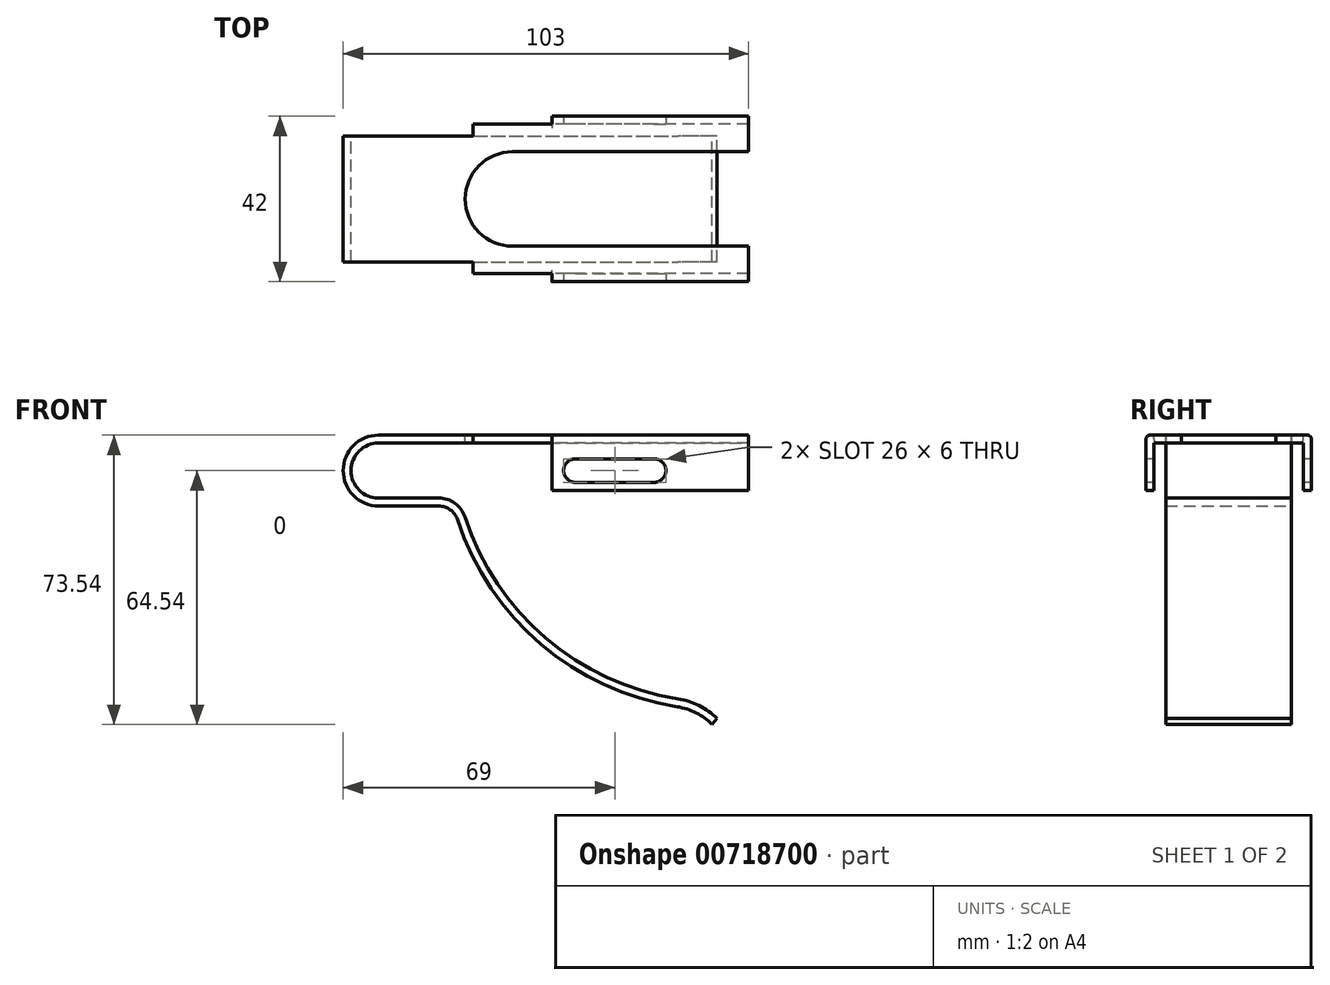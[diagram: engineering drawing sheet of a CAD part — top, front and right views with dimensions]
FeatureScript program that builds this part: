
annotation { "Feature Type Name" : "Feature", "Feature Type Description" : "" }
export const myFeature = defineFeature(function(context is Context, id is Id, definition is map)
    precondition{}
    {
        {
            var Q0;
            Q0=qCreatedBy(makeId("Front.planeOp"),FACE);
            var sketch = newSketch(context, id + "F0", { "sketchPlane" : qUnion([Q0])});
            skArc(sketch, "E0", {"start": v(0, 9) * mm, "mid": v(-9, 0) * mm, "end": v(0, -9) * mm});
            skLineSegment(sketch, "E1", {"start": v(0, 9) * mm, "end": v(94, 9) * mm});
            skLineSegment(sketch, "E2", {"start": v(0, -9) * mm, "end": v(15.27, -9) * mm});
            skArc(sketch, "E3", {"start": v(20.03, -12.45) * mm, "mid": v(41.23, -44.13) * mm, "end": v(75.88, -60) * mm});
            skArc(sketch, "E4", {"start": v(84.72, -64.54) * mm, "mid": v(80.66, -61.56) * mm, "end": v(75.88, -60) * mm});
            skPoint(sketch, "E5.visualSharp", {"position": v(19, -9) * mm});
            skArc(sketch, "E5.filletArc", {"start": v(20.03, -12.45) * mm, "mid": v(18.2, -9.95) * mm, "end": v(15.27, -9) * mm});
            skLineSegment(sketch, "E6.0", {"start": v(0, 7) * mm, "end": v(94, 7) * mm});
            skArc(sketch, "E6.1", {"start": v(0, 7) * mm, "mid": v(-7, 0) * mm, "end": v(0, -7) * mm});
            skArc(sketch, "E6.2", {"start": v(86, -63) * mm, "mid": v(81.43, -59.71) * mm, "end": v(76.05, -58) * mm});
            skArc(sketch, "E6.3", {"start": v(21.93, -11.84) * mm, "mid": v(42.47, -42.56) * mm, "end": v(76.05, -58) * mm});
            skArc(sketch, "E6.4", {"start": v(21.93, -11.84) * mm, "mid": v(19.38, -8.34) * mm, "end": v(15.27, -7) * mm});
            skLineSegment(sketch, "E6.5", {"start": v(0, -7) * mm, "end": v(15.27, -7) * mm});
            skLineSegment(sketch, "E7", {"start": v(94, 7) * mm, "end": v(94, 9) * mm});
            skLineSegment(sketch, "E8", {"start": v(86, -63) * mm, "end": v(84.72, -64.54) * mm});
            skSolve(sketch);
        }
        {
            var Q0;
            Q0 = qSketchRegion(id + "F0", true);
            extrude(context, id + "F1", {"entities" : qUnion([Q0]), "depth" : 16 * mm, "offsetDistance" : 25 * mm});
        }
        {
            var Q0;
            Q0=makeQuery(id+"F1.opExtrude","SWEPT_FACE",FACE,{"disambiguationData":[OSD([sQuery(id+"F0.wireOp",EDGE,"E1")])]});
            var sketch = newSketch(context, id + "F2", { "sketchPlane" : qUnion([Q0])});
            skLineSegment(sketch, "E9.bottom", {"start": v(94, -16) * mm, "end": v(24, -16) * mm});
            skLineSegment(sketch, "E9.top", {"start": v(94, -19) * mm, "end": v(24, -19) * mm});
            skLineSegment(sketch, "E9.left", {"start": v(94, -16) * mm, "end": v(94, -19) * mm});
            skLineSegment(sketch, "E9.right", {"start": v(24, -16) * mm, "end": v(24, -19) * mm});
            skSolve(sketch);
        }
        {
            var Q0;
            Q0 = qSketchRegion(id + "F2", true);
            extrude(context, id + "F3", {"entities" : qUnion([Q0]), "operationType" : NewBodyOperationType.ADD, "oppositeDirection" : true, "depth" : 2 * mm, "offsetDistance" : 25 * mm});
        }
        {
            var Q0;
            Q0=makeQuery(id+"F3.opExtrude","SWEPT_FACE",FACE,{"disambiguationData":[OSD([sQuery(id+"F2.wireOp",EDGE,"E9.top")])]});
            var sketch = newSketch(context, id + "F4", { "sketchPlane" : qUnion([Q0])});
            skLineSegment(sketch, "E10.bottom", {"start": v(94, 9) * mm, "end": v(44, 9) * mm});
            skLineSegment(sketch, "E10.top", {"start": v(94, -5) * mm, "end": v(44, -5) * mm});
            skLineSegment(sketch, "E10.left", {"start": v(94, 9) * mm, "end": v(94, -5) * mm});
            skLineSegment(sketch, "E10.right", {"start": v(44, 9) * mm, "end": v(44, -5) * mm});
            skSolve(sketch);
        }
        {
            var Q0;
            Q0 = qSketchRegion(id + "F4", true);
            extrude(context, id + "F5", {"entities" : qUnion([Q0]), "operationType" : NewBodyOperationType.ADD, "depth" : 2 * mm, "offsetDistance" : 25 * mm});
        }
        {
            var Q0;
            Q0=makeQuery(id+"F5.opExtrude","CAP_EDGE",EDGE,{"disambiguationData":[OSD([sQuery(id+"F4.wireOp",EDGE,"E10.bottom")])],"isStart":false});
            var Q1;
            {var subQ0=sQuery(id+"F2.wireOp",EDGE,"E9.top");Q1=makeQuery(id+"F5.boolean.opBoolean","SPLIT",EDGE,{"disambiguationData":[topologyDisambiguationEdgeConnected([makeQuery(id+"F5.opExtrude","CAP_FACE",FACE,{"disambiguationData":[OSD([sQuery(id+"F4.wireOp",EDGE,"E10.bottom"),sQuery(id+"F4.wireOp",EDGE,"E10.top"),sQuery(id+"F4.wireOp",EDGE,"E10.left"),sQuery(id+"F4.wireOp",EDGE,"E10.right")])],"isStart":true})])],"derivedFrom":makeQuery(id+"F3.opExtrude","CAP_EDGE",EDGE,{"disambiguationData":[OSD([subQ0])],"isStart":false})});}
            fillet(context, id + "F6", {"entities" : qUnion([Q0, Q1]), "radius" : 1 * mm, "allowEdgeOverflow" : false});
        }
        {
            var Q0;
            Q0=makeQuery(id+"F1.opExtrude","SWEPT_BODY",BODY,{"disambiguationData":[OSD([sQuery(id+"F0.wireOp",EDGE,"E0"),sQuery(id+"F0.wireOp",EDGE,"E1"),sQuery(id+"F0.wireOp",EDGE,"E2"),sQuery(id+"F0.wireOp",EDGE,"E3"),sQuery(id+"F0.wireOp",EDGE,"E4"),sQuery(id+"F0.wireOp",EDGE,"E5.filletArc"),sQuery(id+"F0.wireOp",EDGE,"E6.0"),sQuery(id+"F0.wireOp",EDGE,"E6.1"),sQuery(id+"F0.wireOp",EDGE,"E6.2"),sQuery(id+"F0.wireOp",EDGE,"E6.3"),sQuery(id+"F0.wireOp",EDGE,"E6.4"),sQuery(id+"F0.wireOp",EDGE,"E6.5"),sQuery(id+"F0.wireOp",EDGE,"E7"),sQuery(id+"F0.wireOp",EDGE,"E8")])]});
            var Q1;
            Q1=qCreatedBy(makeId("Front.planeOp"),FACE);
            mirror(context, id + "F7", {"operationType" : NewBodyOperationType.ADD, "entities" : qUnion([Q0]), "mirrorPlane" : qUnion([Q1])});
        }
        {
            var Q0;
            {var subQ0=makeQuery(id+"F5.boolean.opBoolean","MERGE",FACE,{"derivedFrom":[makeQuery(id+"F3.boolean.opBoolean","MERGE",FACE,{"derivedFrom":[makeQuery(id+"F1.opExtrude","SWEPT_FACE",FACE,{"disambiguationData":[OSD([sQuery(id+"F0.wireOp",EDGE,"E1")])]}),makeQuery(id+"F3.opExtrude","CAP_FACE",FACE,{"disambiguationData":[OSD([sQuery(id+"F2.wireOp",EDGE,"E9.bottom"),sQuery(id+"F2.wireOp",EDGE,"E9.top"),sQuery(id+"F2.wireOp",EDGE,"E9.left"),sQuery(id+"F2.wireOp",EDGE,"E9.right")])],"isStart":true})]}),makeQuery(id+"F5.opExtrude","SWEPT_FACE",FACE,{"disambiguationData":[OSD([sQuery(id+"F4.wireOp",EDGE,"E10.bottom")])]})]});Q0=makeQuery(id+"F7.boolean.opBoolean","MERGE",FACE,{"derivedFrom":[subQ0,makeQuery(id+"F7.opPattern","COPY",FACE,{"derivedFrom":subQ0,"instanceName":"1"})]});}
            var sketch = newSketch(context, id + "F8", { "sketchPlane" : qUnion([Q0])});
            skArc(sketch, "E11", {"start": v(34, 12) * mm, "mid": v(22, 0) * mm, "end": v(34, -12) * mm});
            skLineSegment(sketch, "E12", {"start": v(34, 12) * mm, "end": v(94, 12) * mm});
            skLineSegment(sketch, "E13", {"start": v(34, -12) * mm, "end": v(94, -12) * mm});
            skSolve(sketch);
        }
        {
            var Q0;
            Q0=makeQuery(id+"F8.imprint","IMPRINT",FACE,{"disambiguationData":[TD([[makeQuery(id+"F8.imprint","IMPRINT",EDGE,{"derivedFrom":sQuery(id+"F8.wireOp",EDGE,"E11")}),1.0]])]});
            extrude(context, id + "F9", {"entities" : qUnion([Q0]), "operationType" : NewBodyOperationType.REMOVE, "oppositeDirection" : true, "depth" : 2 * mm, "offsetDistance" : 25 * mm});
        }
        {
            var Q0;
            Q0=makeQuery(id+"F5.opExtrude","CAP_FACE",FACE,{"disambiguationData":[OSD([sQuery(id+"F4.wireOp",EDGE,"E10.bottom"),sQuery(id+"F4.wireOp",EDGE,"E10.top"),sQuery(id+"F4.wireOp",EDGE,"E10.left"),sQuery(id+"F4.wireOp",EDGE,"E10.right")])],"isStart":false});
            var sketch = newSketch(context, id + "F10", { "sketchPlane" : qUnion([Q0])});
            skLineSegment(sketch, "E14", {"start": v(50, 0) * mm, "end": v(70, 0) * mm});
            skArc(sketch, "E15.0.startCap", {"start": v(50, -3) * mm, "mid": v(47, 0) * mm, "end": v(50, 3) * mm});
            skArc(sketch, "E15.0.endCap", {"start": v(70, 3) * mm, "mid": v(73, 0) * mm, "end": v(70, -3) * mm});
            skLineSegment(sketch, "E15.0.left", {"start": v(50, 3) * mm, "end": v(70, 3) * mm});
            skLineSegment(sketch, "E15.0.right", {"start": v(50, -3) * mm, "end": v(70, -3) * mm});
            skSolve(sketch);
        }
        {
            var Q0;
            Q0 = qSketchRegion(id + "F10", true);
            extrude(context, id + "F11", {"entities" : qUnion([Q0]), "operationType" : NewBodyOperationType.REMOVE, "endBound" : BoundingType.THROUGH_ALL, "oppositeDirection" : true, "depth" : 25 * mm, "offsetDistance" : 25 * mm});
        }
    });
